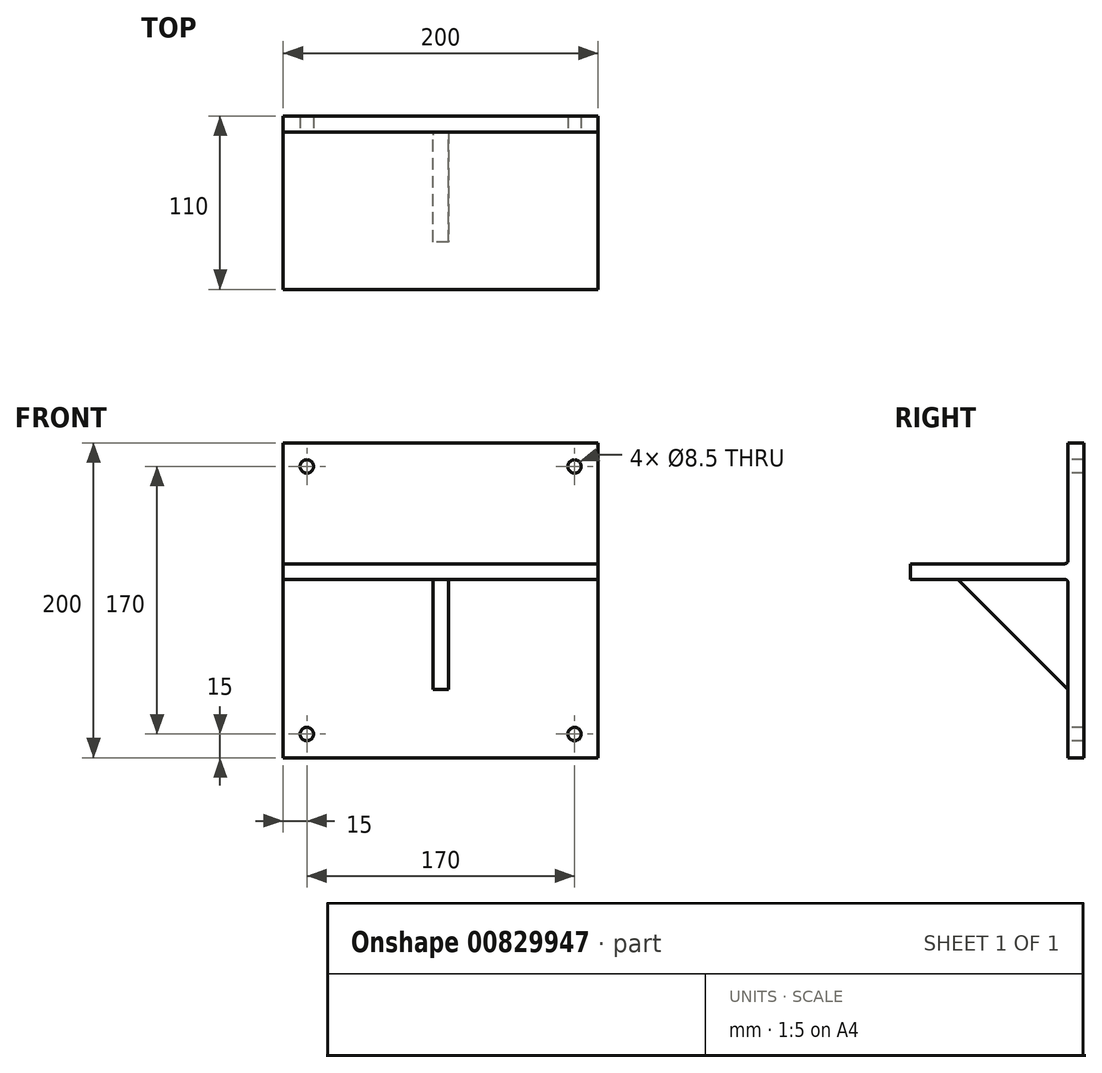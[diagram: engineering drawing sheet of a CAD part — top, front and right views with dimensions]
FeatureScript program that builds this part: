
annotation { "Feature Type Name" : "Feature", "Feature Type Description" : "" }
export const myFeature = defineFeature(function(context is Context, id is Id, definition is map)
    precondition{}
    {
        {
            var Q0;
            Q0=qCreatedBy(makeId("Right.planeOp"),FACE);
            var sketch = newSketch(context, id + "F0", { "sketchPlane" : qUnion([Q0])});
            skLineSegment(sketch, "E0.bottom", {"start": v(5, 100) * mm, "end": v(-5, 100) * mm});
            skLineSegment(sketch, "E0.top", {"start": v(5, -100) * mm, "end": v(-5, -100) * mm});
            skLineSegment(sketch, "E0.left", {"start": v(5, 100) * mm, "end": v(5, -100) * mm});
            skLineSegment(sketch, "E0.right", {"start": v(-5, 100) * mm, "end": v(-5, -100) * mm});
            skLineSegment(sketch, "E1.bottom", {"start": v(-5, 23.2) * mm, "end": v(-105, 23.2) * mm});
            skLineSegment(sketch, "E1.top", {"start": v(-5, 13.2) * mm, "end": v(-105, 13.2) * mm});
            skLineSegment(sketch, "E1.left", {"start": v(-5, 23.2) * mm, "end": v(-5, 13.2) * mm});
            skLineSegment(sketch, "E1.right", {"start": v(-105, 23.2) * mm, "end": v(-105, 13.2) * mm});
            skLineSegment(sketch, "E2.bottom", {"start": v(-5, 13.2) * mm, "end": v(-5, 13.2) * mm});
            skLineSegment(sketch, "E2.top", {"start": v(-5, -100) * mm, "end": v(-5, -100) * mm});
            skLineSegment(sketch, "E2.left", {"start": v(-5, 13.2) * mm, "end": v(-5, -100) * mm});
            skLineSegment(sketch, "E2.right", {"start": v(-5, 13.2) * mm, "end": v(-5, -100) * mm});
            skSolve(sketch);
        }
        {
            var Q0;
            {var subQ3=sQuery(id+"F0.wireOp",EDGE,"E0.bottom");Q0=makeQuery(id+"F0.imprint","IMPRINT",FACE,{"disambiguationData":[TD([[makeQuery(id+"F0.imprint","IMPRINT",EDGE,{"derivedFrom":subQ3}),1.0]])]});}
            var Q1;
            {var subQ2=sQuery(id+"F0.wireOp",EDGE,"E1.bottom");Q1=makeQuery(id+"F0.imprint","IMPRINT",FACE,{"disambiguationData":[TD([[makeQuery(id+"F0.imprint","IMPRINT",EDGE,{"derivedFrom":subQ2}),1.0]])]});}
            extrude(context, id + "F1", {"entities" : qUnion([Q0, Q1]), "depth" : 200 * mm, "offsetDistance" : 25 * mm});
        }
        {
            var Q0;
            {var subQ0=sQuery(id+"F0.wireOp",EDGE,"E0.right");Q0=makeQuery(id+"F1.opExtrude","SWEPT_FACE",FACE,{"disambiguationData":[OSD([subQ0]),TDD([makeQuery(id+"F0.imprint","IMPRINT",EDGE,{"disambiguationData":[TD([[makeQuery(id+"F0.imprint","INTERSECT",VERTEX,{"derivedFrom":[sQuery(id+"F0.wireOp",EDGE,"E0.top"),subQ0]}),1.0]])],"derivedFrom":subQ0})])]});}
            var sketch = newSketch(context, id + "F2", { "sketchPlane" : qUnion([Q0])});
            skLineSegment(sketch, "E3.bottom", {"start": v(95, 13.2) * mm, "end": v(105, 13.2) * mm});
            skLineSegment(sketch, "E3.top", {"start": v(95, -56.8) * mm, "end": v(105, -56.8) * mm});
            skLineSegment(sketch, "E3.left", {"start": v(95, 13.2) * mm, "end": v(95, -56.8) * mm});
            skLineSegment(sketch, "E3.right", {"start": v(105, 13.2) * mm, "end": v(105, -56.8) * mm});
            skSolve(sketch);
        }
        {
            var Q0;
            Q0=makeQuery(id+"F2.imprint","IMPRINT",FACE,{"disambiguationData":[TD([[makeQuery(id+"F2.imprint","IMPRINT",EDGE,{"derivedFrom":sQuery(id+"F2.wireOp",EDGE,"E3.bottom")}),1.0]])]});
            extrude(context, id + "F3", {"entities" : qUnion([Q0]), "operationType" : NewBodyOperationType.ADD, "depth" : 70 * mm, "offsetDistance" : 25 * mm});
        }
        {
            var Q0;
            Q0=makeQuery(id+"F3.opExtrude","SWEPT_FACE",FACE,{"disambiguationData":[OSD([sQuery(id+"F2.wireOp",EDGE,"E3.left")])]});
            var sketch = newSketch(context, id + "F4", { "sketchPlane" : qUnion([Q0])});
            skLineSegment(sketch, "E4", {"start": v(75, 13.2) * mm, "end": v(5, -56.8) * mm});
            skSolve(sketch);
        }
        {
            var Q0;
            Q0=makeQuery(id+"F4.imprint","IMPRINT",FACE,{"disambiguationData":[TD([[makeQuery(id+"F4.imprint","IMPRINT",EDGE,{"derivedFrom":sQuery(id+"F4.wireOp",EDGE,"E4")}),1.0]])]});
            extrude(context, id + "F5", {"entities" : qUnion([Q0]), "operationType" : NewBodyOperationType.REMOVE, "oppositeDirection" : true, "depth" : 70 * mm, "offsetDistance" : 25 * mm});
        }
        {
            var Q0;
            {var subQ0=sQuery(id+"F0.wireOp",EDGE,"E0.right");Q0=makeQuery(id+"F1.opExtrude","SWEPT_FACE",FACE,{"disambiguationData":[OSD([subQ0]),TDD([makeQuery(id+"F0.imprint","IMPRINT",EDGE,{"disambiguationData":[TD([[makeQuery(id+"F0.imprint","INTERSECT",VERTEX,{"derivedFrom":[sQuery(id+"F0.wireOp",EDGE,"E0.bottom"),subQ0]}),-1.0]])],"derivedFrom":subQ0})])]});}
            var sketch = newSketch(context, id + "F6", { "sketchPlane" : qUnion([Q0])});
            skLineSegment(sketch, "E5.bottom", {"start": v(15, 85) * mm, "end": v(185, 85) * mm});
            skLineSegment(sketch, "E5.top", {"start": v(15, -85) * mm, "end": v(185, -85) * mm});
            skLineSegment(sketch, "E5.left", {"start": v(15, 85) * mm, "end": v(15, -85) * mm});
            skLineSegment(sketch, "E5.right", {"start": v(185, 85) * mm, "end": v(185, -85) * mm});
            skCircle(sketch, "E6", {"center": v(15, 85) * mm, "radius": 4.25 * mm});
            skCircle(sketch, "E7", {"center": v(185, 85) * mm, "radius": 4.25 * mm});
            skCircle(sketch, "E8", {"center": v(185, -85) * mm, "radius": 4.25 * mm});
            skCircle(sketch, "E9", {"center": v(15, -85) * mm, "radius": 4.25 * mm});
            skSolve(sketch);
        }
        {
            var Q0;
            {var subQ0=sQuery(id+"F6.wireOp",EDGE,"E5.left");var subQ1=sQuery(id+"F6.wireOp",EDGE,"E5.bottom");var subQ2=makeQuery(id+"F6.imprint","INTERSECT",VERTEX,{"derivedFrom":[subQ1,subQ0]});Q0=makeQuery(id+"F6.imprint","IMPRINT",FACE,{"disambiguationData":[TD([[makeQuery(id+"F6.imprint","IMPRINT",EDGE,{"disambiguationData":[TD([[subQ2,-1.0]])],"derivedFrom":subQ1}),1.0]])]});}
            var Q1;
            {var subQ0=sQuery(id+"F6.wireOp",EDGE,"E5.left");var subQ1=sQuery(id+"F6.wireOp",EDGE,"E5.bottom");var subQ2=makeQuery(id+"F6.imprint","INTERSECT",VERTEX,{"derivedFrom":[subQ1,subQ0]});Q1=makeQuery(id+"F6.imprint","IMPRINT",FACE,{"disambiguationData":[TD([[makeQuery(id+"F6.imprint","IMPRINT",EDGE,{"disambiguationData":[TD([[subQ2,-1.0]])],"derivedFrom":subQ1}),-1.0]])]});}
            var Q2;
            {var subQ0=sQuery(id+"F6.wireOp",EDGE,"E5.right");var subQ1=sQuery(id+"F6.wireOp",EDGE,"E5.bottom");var subQ2=makeQuery(id+"F6.imprint","INTERSECT",VERTEX,{"derivedFrom":[subQ1,subQ0]});Q2=makeQuery(id+"F6.imprint","IMPRINT",FACE,{"disambiguationData":[TD([[makeQuery(id+"F6.imprint","IMPRINT",EDGE,{"disambiguationData":[TD([[subQ2,1.0]])],"derivedFrom":subQ1}),1.0]])]});}
            var Q3;
            {var subQ0=sQuery(id+"F6.wireOp",EDGE,"E5.right");var subQ1=sQuery(id+"F6.wireOp",EDGE,"E5.bottom");var subQ2=makeQuery(id+"F6.imprint","INTERSECT",VERTEX,{"derivedFrom":[subQ1,subQ0]});Q3=makeQuery(id+"F6.imprint","IMPRINT",FACE,{"disambiguationData":[TD([[makeQuery(id+"F6.imprint","IMPRINT",EDGE,{"disambiguationData":[TD([[subQ2,1.0]])],"derivedFrom":subQ1}),-1.0]])]});}
            var Q4;
            {var subQ0=sQuery(id+"F6.wireOp",EDGE,"E5.right");var subQ1=sQuery(id+"F6.wireOp",EDGE,"E5.top");var subQ2=makeQuery(id+"F6.imprint","INTERSECT",VERTEX,{"derivedFrom":[subQ1,subQ0]});Q4=makeQuery(id+"F6.imprint","IMPRINT",FACE,{"disambiguationData":[TD([[makeQuery(id+"F6.imprint","IMPRINT",EDGE,{"disambiguationData":[TD([[subQ2,1.0]])],"derivedFrom":subQ1}),-1.0]])]});}
            var Q5;
            {var subQ0=sQuery(id+"F6.wireOp",EDGE,"E5.right");var subQ1=sQuery(id+"F6.wireOp",EDGE,"E5.top");var subQ2=makeQuery(id+"F6.imprint","INTERSECT",VERTEX,{"derivedFrom":[subQ1,subQ0]});Q5=makeQuery(id+"F6.imprint","IMPRINT",FACE,{"disambiguationData":[TD([[makeQuery(id+"F6.imprint","IMPRINT",EDGE,{"disambiguationData":[TD([[subQ2,1.0]])],"derivedFrom":subQ1}),1.0]])]});}
            var Q6;
            {var subQ0=sQuery(id+"F6.wireOp",EDGE,"E5.left");var subQ1=sQuery(id+"F6.wireOp",EDGE,"E5.top");var subQ2=makeQuery(id+"F6.imprint","INTERSECT",VERTEX,{"derivedFrom":[subQ1,subQ0]});Q6=makeQuery(id+"F6.imprint","IMPRINT",FACE,{"disambiguationData":[TD([[makeQuery(id+"F6.imprint","IMPRINT",EDGE,{"disambiguationData":[TD([[subQ2,-1.0]])],"derivedFrom":subQ1}),-1.0]])]});}
            var Q7;
            {var subQ0=sQuery(id+"F6.wireOp",EDGE,"E5.left");var subQ1=sQuery(id+"F6.wireOp",EDGE,"E5.top");var subQ2=makeQuery(id+"F6.imprint","INTERSECT",VERTEX,{"derivedFrom":[subQ1,subQ0]});Q7=makeQuery(id+"F6.imprint","IMPRINT",FACE,{"disambiguationData":[TD([[makeQuery(id+"F6.imprint","IMPRINT",EDGE,{"disambiguationData":[TD([[subQ2,-1.0]])],"derivedFrom":subQ1}),1.0]])]});}
            extrude(context, id + "F7", {"entities" : qUnion([Q0, Q1, Q2, Q3, Q4, Q5, Q6, Q7]), "operationType" : NewBodyOperationType.REMOVE, "oppositeDirection" : true, "depth" : 20 * mm, "offsetDistance" : 25 * mm});
        }
        {
            var Q0;
            Q0=makeQuery(id+"F1.opExtrude","SWEPT_EDGE",EDGE,{"disambiguationData":[OSD([sQuery(id+"F0.wireOp",EDGE,"E0.right"),sQuery(id+"F0.wireOp",EDGE,"E1.bottom")])]});
            var Q1;
            {var subQ0=sQuery(id+"F0.wireOp",EDGE,"E1.top");var subQ1=sQuery(id+"F0.wireOp",EDGE,"E0.right");Q1=makeQuery(id+"F3.boolean.opBoolean","SPLIT",EDGE,{"disambiguationData":[TD([makeQuery(id+"F3.opExtrude","SWEPT_FACE",FACE,{"disambiguationData":[OSD([sQuery(id+"F2.wireOp",EDGE,"E3.left")])]})])],"derivedFrom":makeQuery(id+"F1.opExtrude","SWEPT_EDGE",EDGE,{"disambiguationData":[OSD([subQ1,subQ0])]})});}
            var Q2;
            {var subQ0=sQuery(id+"F0.wireOp",EDGE,"E1.top");var subQ1=sQuery(id+"F0.wireOp",EDGE,"E0.right");Q2=makeQuery(id+"F3.boolean.opBoolean","SPLIT",EDGE,{"disambiguationData":[TD([makeQuery(id+"F3.opExtrude","SWEPT_FACE",FACE,{"disambiguationData":[OSD([sQuery(id+"F2.wireOp",EDGE,"E3.right")])]})])],"derivedFrom":makeQuery(id+"F1.opExtrude","SWEPT_EDGE",EDGE,{"disambiguationData":[OSD([subQ1,subQ0])]})});}
            var Q3;
            Q3=makeQuery(id+"F3.opExtrude","SWEPT_EDGE",EDGE,{"disambiguationData":[OSD([sQuery(id+"F0.wireOp",EDGE,"E0.right"),sQuery(id+"F0.wireOp",EDGE,"E1.top"),sQuery(id+"F2.wireOp",EDGE,"E3.bottom"),sQuery(id+"F2.wireOp",EDGE,"E3.right")])]});
            var Q4;
            Q4=makeQuery(id+"F3.opExtrude","CAP_EDGE",EDGE,{"disambiguationData":[OSD([sQuery(id+"F2.wireOp",EDGE,"E3.right")])],"isStart":true});
            var Q5;
            Q5=makeQuery(id+"F3.opExtrude","CAP_EDGE",EDGE,{"disambiguationData":[OSD([sQuery(id+"F2.wireOp",EDGE,"E3.left")])],"isStart":true});
            var Q6;
            Q6=makeQuery(id+"F3.opExtrude","SWEPT_EDGE",EDGE,{"disambiguationData":[OSD([sQuery(id+"F0.wireOp",EDGE,"E0.right"),sQuery(id+"F0.wireOp",EDGE,"E1.top"),sQuery(id+"F2.wireOp",EDGE,"E3.bottom"),sQuery(id+"F2.wireOp",EDGE,"E3.left")])]});
            fillet(context, id + "F8", {"entities" : qUnion([Q0, Q1, Q2, Q3, Q4, Q5, Q6]), "radius" : 2 * mm, "tangentPropagation" : true, "allowEdgeOverflow" : false});
        }
    });
